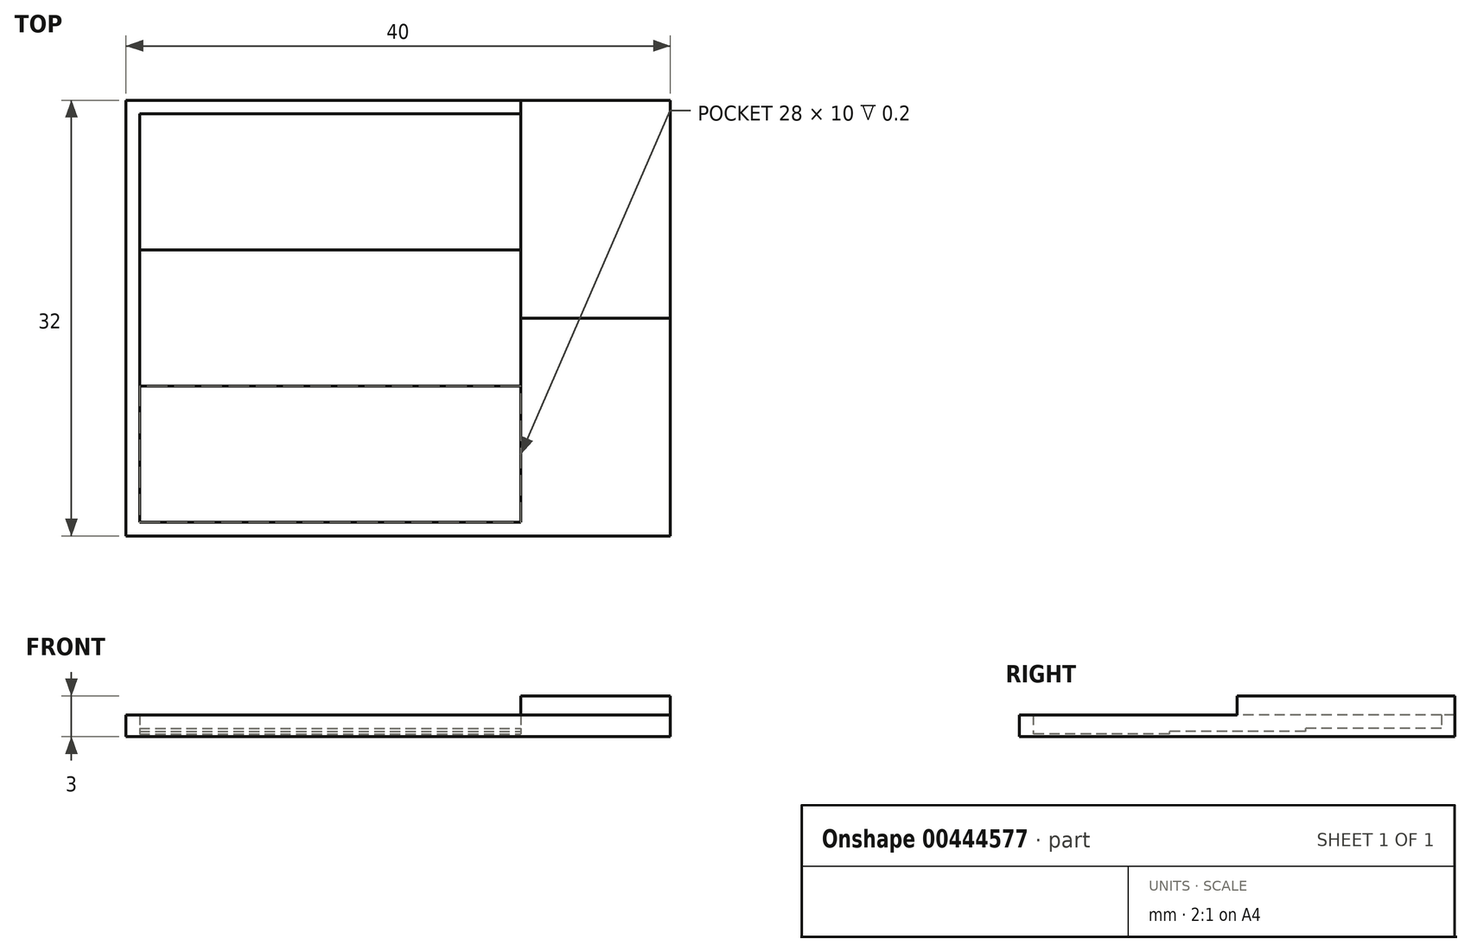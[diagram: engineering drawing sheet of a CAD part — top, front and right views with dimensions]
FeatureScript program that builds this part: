
annotation { "Feature Type Name" : "Feature", "Feature Type Description" : "" }
export const myFeature = defineFeature(function(context is Context, id is Id, definition is map)
    precondition{}
    {
        {
            var Q0;
            Q0=qCreatedBy(makeId("Top.planeOp"),FACE);
            var sketch = newSketch(context, id + "F0", { "sketchPlane" : qUnion([Q0])});
            skLineSegment(sketch, "E0.bottom", {"start": v(0, 0) * mm, "end": v(30, 0) * mm});
            skLineSegment(sketch, "E0.top", {"start": v(0, -32) * mm, "end": v(30, -32) * mm});
            skLineSegment(sketch, "E0.left", {"start": v(0, 0) * mm, "end": v(0, -32) * mm});
            skLineSegment(sketch, "E0.right", {"start": v(30, 0) * mm, "end": v(30, -32) * mm});
            skSolve(sketch);
        }
        {
            var Q0;
            Q0=makeQuery(id+"F0.imprint","IMPRINT",FACE,{"disambiguationData":[TD([[makeQuery(id+"F0.imprint","IMPRINT",EDGE,{"derivedFrom":sQuery(id+"F0.wireOp",EDGE,"E0.bottom")}),-1.0]])]});
            extrude(context, id + "F1", {"entities" : qUnion([Q0]), "depth" : 0.2 * mm, "offsetDistance" : 25 * mm});
        }
        {
            var Q0;
            Q0=makeQuery(id+"F1.opExtrude","CAP_FACE",FACE,{"disambiguationData":[OSD([sQuery(id+"F0.wireOp",EDGE,"E0.bottom"),sQuery(id+"F0.wireOp",EDGE,"E0.top"),sQuery(id+"F0.wireOp",EDGE,"E0.left"),sQuery(id+"F0.wireOp",EDGE,"E0.right")])],"isStart":false});
            var sketch = newSketch(context, id + "F2", { "sketchPlane" : qUnion([Q0])});
            skLineSegment(sketch, "E1.bottom", {"start": v(1, -1) * mm, "end": v(29, -1) * mm});
            skLineSegment(sketch, "E1.top", {"start": v(1, -31) * mm, "end": v(29, -31) * mm});
            skLineSegment(sketch, "E1.left", {"start": v(1, -1) * mm, "end": v(1, -31) * mm});
            skLineSegment(sketch, "E1.right", {"start": v(29, -1) * mm, "end": v(29, -31) * mm});
            skSolve(sketch);
        }
        {
            var Q0;
            Q0=makeQuery(id+"F2.imprint","IMPRINT",FACE,{"disambiguationData":[TD([[makeQuery(id+"F2.imprint","IMPRINT",EDGE,{"derivedFrom":sQuery(id+"F2.wireOp",EDGE,"E1.bottom")}),1.0]])]});
            extrude(context, id + "F3", {"entities" : qUnion([Q0]), "operationType" : NewBodyOperationType.ADD, "depth" : 1.4 * mm, "offsetDistance" : 25 * mm});
        }
        {
            var Q0;
            Q0=makeQuery(id+"F1.opExtrude","CAP_FACE",FACE,{"disambiguationData":[OSD([sQuery(id+"F0.wireOp",EDGE,"E0.bottom"),sQuery(id+"F0.wireOp",EDGE,"E0.top"),sQuery(id+"F0.wireOp",EDGE,"E0.left"),sQuery(id+"F0.wireOp",EDGE,"E0.right")])],"isStart":false});
            var sketch = newSketch(context, id + "F4", { "sketchPlane" : qUnion([Q0])});
            skLineSegment(sketch, "E2.bottom", {"start": v(1, -1) * mm, "end": v(29, -1) * mm});
            skLineSegment(sketch, "E2.top", {"start": v(1, -21) * mm, "end": v(29, -21) * mm});
            skLineSegment(sketch, "E2.left", {"start": v(1, -1) * mm, "end": v(1, -21) * mm});
            skLineSegment(sketch, "E2.right", {"start": v(29, -1) * mm, "end": v(29, -21) * mm});
            skSolve(sketch);
        }
        {
            var Q0;
            Q0=makeQuery(id+"F4.imprint","IMPRINT",FACE,{"disambiguationData":[TD([[makeQuery(id+"F4.imprint","IMPRINT",EDGE,{"derivedFrom":sQuery(id+"F4.wireOp",EDGE,"E2.bottom")}),-1.0]])]});
            extrude(context, id + "F5", {"entities" : qUnion([Q0]), "operationType" : NewBodyOperationType.ADD, "depth" : 0.2 * mm, "offsetDistance" : 25 * mm});
        }
        {
            var Q0;
            Q0=makeQuery(id+"F5.opExtrude","CAP_FACE",FACE,{"disambiguationData":[OSD([sQuery(id+"F4.wireOp",EDGE,"E2.bottom"),sQuery(id+"F4.wireOp",EDGE,"E2.top"),sQuery(id+"F4.wireOp",EDGE,"E2.left"),sQuery(id+"F4.wireOp",EDGE,"E2.right")])],"isStart":false});
            var sketch = newSketch(context, id + "F6", { "sketchPlane" : qUnion([Q0])});
            skLineSegment(sketch, "E3.bottom", {"start": v(1, -1) * mm, "end": v(29, -1) * mm});
            skLineSegment(sketch, "E3.top", {"start": v(1, -11) * mm, "end": v(29, -11) * mm});
            skLineSegment(sketch, "E3.left", {"start": v(1, -1) * mm, "end": v(1, -11) * mm});
            skLineSegment(sketch, "E3.right", {"start": v(29, -1) * mm, "end": v(29, -11) * mm});
            skSolve(sketch);
        }
        {
            var Q0;
            Q0=makeQuery(id+"F6.imprint","IMPRINT",FACE,{"disambiguationData":[TD([[makeQuery(id+"F6.imprint","IMPRINT",EDGE,{"derivedFrom":sQuery(id+"F6.wireOp",EDGE,"E3.bottom")}),-1.0]])]});
            extrude(context, id + "F7", {"entities" : qUnion([Q0]), "operationType" : NewBodyOperationType.ADD, "depth" : 0.2 * mm, "offsetDistance" : 25 * mm});
        }
        {
            var Q0;
            {var subQ0=sQuery(id+"F0.wireOp",EDGE,"E0.right");Q0=makeQuery(id+"F3.boolean.opBoolean","MERGE",FACE,{"derivedFrom":[makeQuery(id+"F1.opExtrude","SWEPT_FACE",FACE,{"disambiguationData":[OSD([subQ0])]}),makeQuery(id+"F3.opExtrude","SWEPT_FACE",FACE,{"disambiguationData":[OSD([subQ0])]})]});}
            extrude(context, id + "F8", {"entities" : qUnion([Q0]), "operationType" : NewBodyOperationType.ADD, "depth" : 10 * mm, "offsetDistance" : 25 * mm});
        }
        {
            var Q0;
            {var subQ0=sQuery(id+"F0.wireOp",EDGE,"E0.right");Q0=makeQuery(id+"F8.boolean.opBoolean","MERGE",FACE,{"derivedFrom":[makeQuery(id+"F3.opExtrude","CAP_FACE",FACE,{"disambiguationData":[OSD([sQuery(id+"F0.wireOp",EDGE,"E0.bottom"),sQuery(id+"F0.wireOp",EDGE,"E0.top"),sQuery(id+"F0.wireOp",EDGE,"E0.left"),subQ0,sQuery(id+"F2.wireOp",EDGE,"E1.bottom"),sQuery(id+"F2.wireOp",EDGE,"E1.top"),sQuery(id+"F2.wireOp",EDGE,"E1.left"),sQuery(id+"F2.wireOp",EDGE,"E1.right")])],"isStart":false}),makeQuery(id+"F8.opExtrude","SWEPT_FACE",FACE,{"disambiguationData":[OSD([subQ0]),TDD([makeQuery(id+"F3.opExtrude","CAP_EDGE",EDGE,{"disambiguationData":[OSD([subQ0])],"isStart":false})])]})]});}
            var sketch = newSketch(context, id + "F9", { "sketchPlane" : qUnion([Q0])});
            skLineSegment(sketch, "E4.bottom", {"start": v(40, 0) * mm, "end": v(29, 0) * mm});
            skLineSegment(sketch, "E4.top", {"start": v(40, -16) * mm, "end": v(29, -16) * mm});
            skLineSegment(sketch, "E4.left", {"start": v(40, 0) * mm, "end": v(40, -16) * mm});
            skLineSegment(sketch, "E4.right", {"start": v(29, 0) * mm, "end": v(29, -16) * mm});
            skSolve(sketch);
        }
        {
            var Q0;
            {var subQ3=sQuery(id+"F9.wireOp",EDGE,"E4.bottom");Q0=makeQuery(id+"F9.imprint","IMPRINT",FACE,{"disambiguationData":[TD([[makeQuery(id+"F9.imprint","IMPRINT",EDGE,{"derivedFrom":subQ3}),-1.0]])]});}
            extrude(context, id + "F10", {"entities" : qUnion([Q0]), "operationType" : NewBodyOperationType.ADD, "depth" : 1.4 * mm, "offsetDistance" : 25 * mm});
        }
    });
